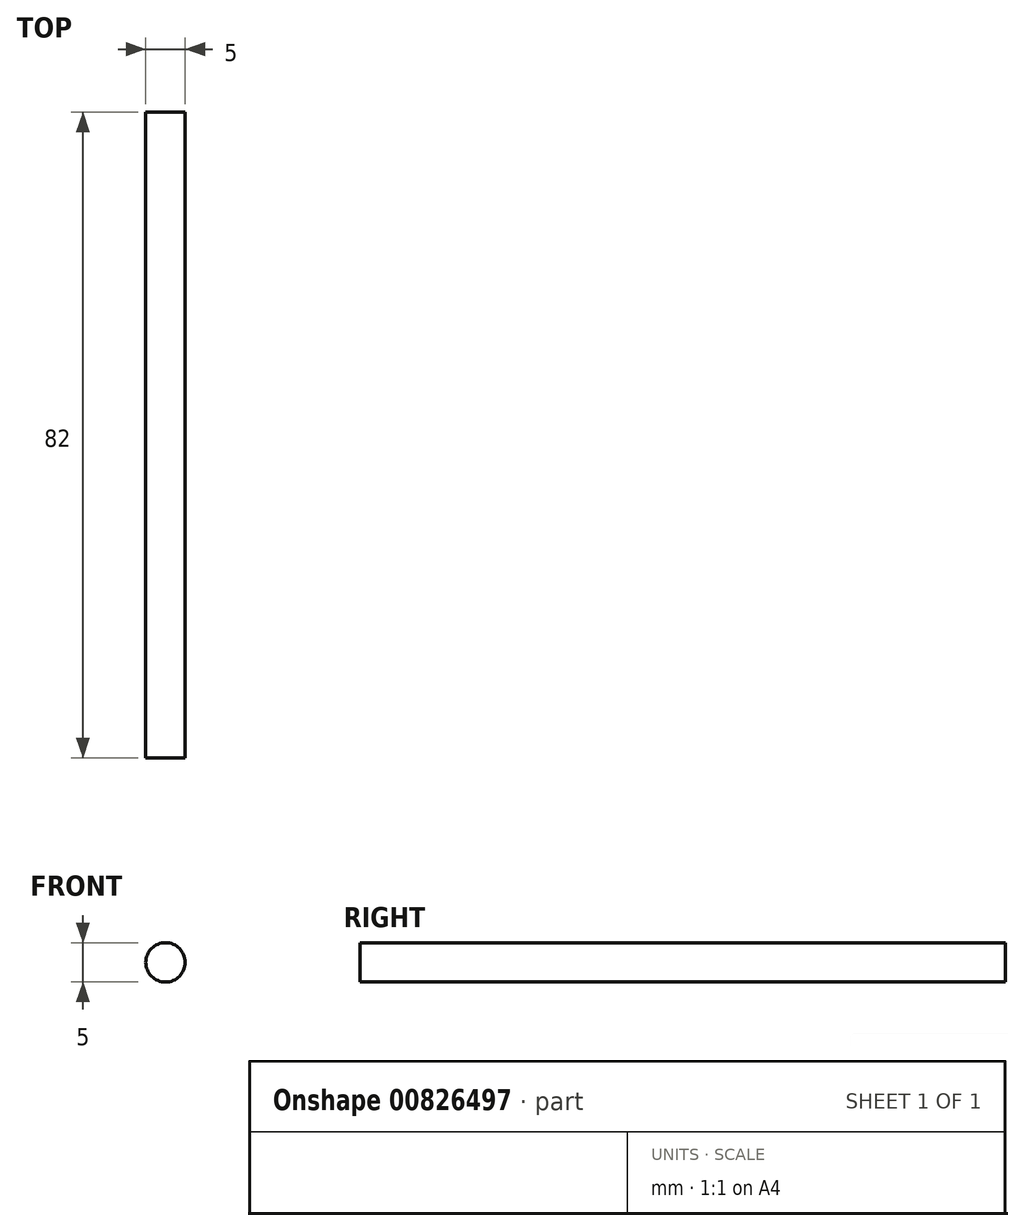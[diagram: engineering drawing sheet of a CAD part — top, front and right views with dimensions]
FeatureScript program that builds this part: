
annotation { "Feature Type Name" : "Feature", "Feature Type Description" : "" }
export const myFeature = defineFeature(function(context is Context, id is Id, definition is map)
    precondition{}
    {
        {
            var Q0;
            Q0=qCreatedBy(makeId("Front.planeOp"),FACE);
            var sketch = newSketch(context, id + "F0", { "sketchPlane" : qUnion([Q0])});
            skCircle(sketch, "E0", {"center": v(0, 0) * mm, "radius": 2.5 * mm});
            skSolve(sketch);
        }
        {
            var Q0;
            Q0 = qSketchRegion(id + "F0", true);
            extrude(context, id + "F1", {"entities" : qUnion([Q0]), "depth" : 82 * mm, "offsetDistance" : 25 * mm});
        }
    });
